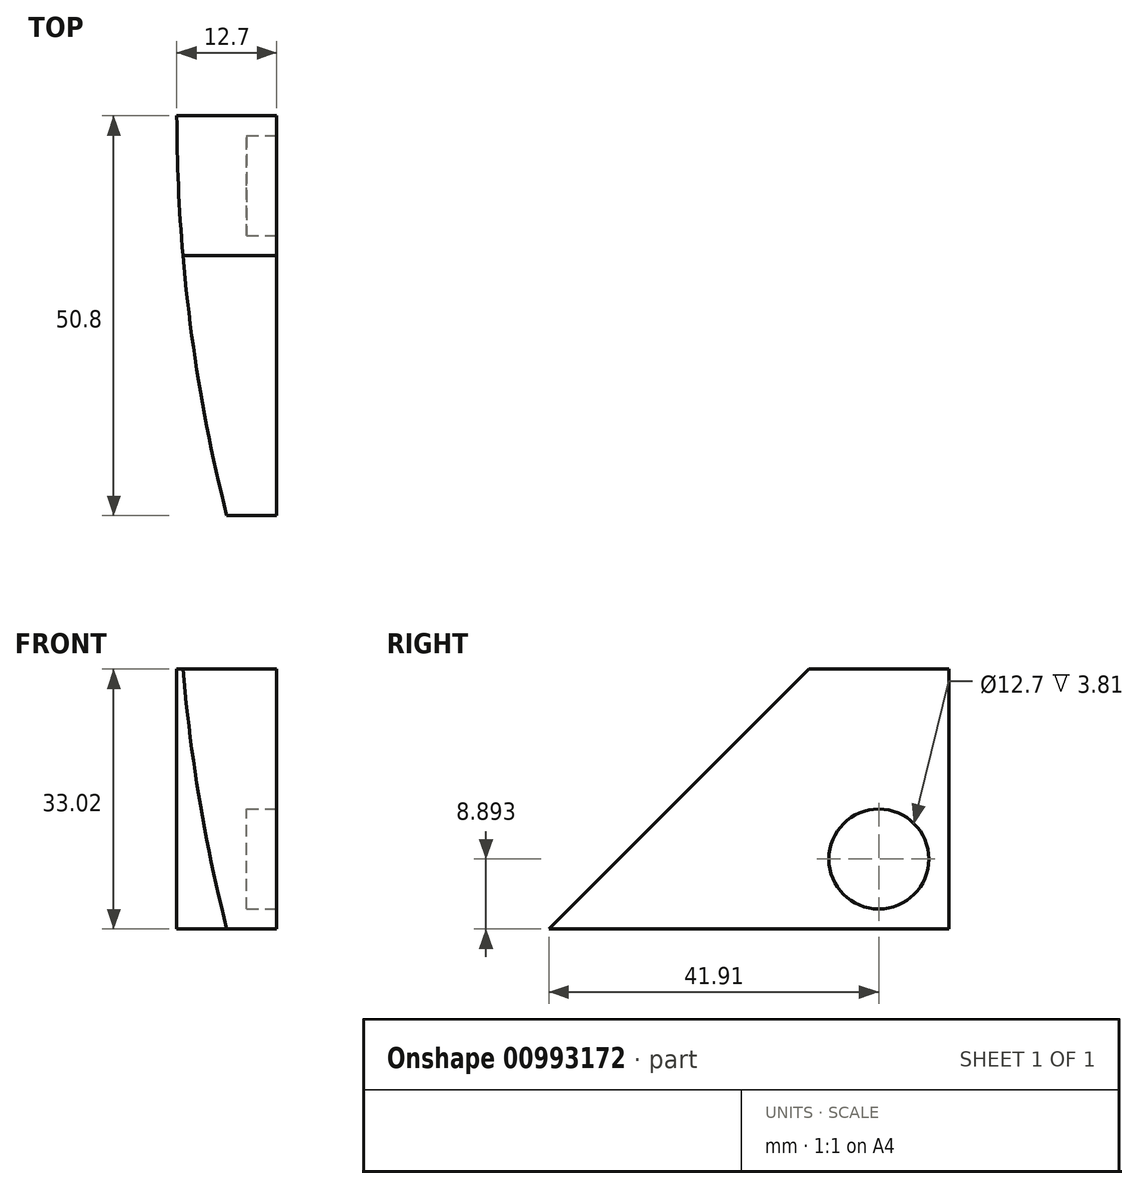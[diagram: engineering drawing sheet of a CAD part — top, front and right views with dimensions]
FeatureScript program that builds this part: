
annotation { "Feature Type Name" : "Feature", "Feature Type Description" : "" }
export const myFeature = defineFeature(function(context is Context, id is Id, definition is map)
    precondition{}
    {
        {
            var Q0;
            Q0=qCreatedBy(makeId("Right.planeOp"),FACE);
            var sketch = newSketch(context, id + "F0", { "sketchPlane" : qUnion([Q0])});
            skCircle(sketch, "E0", {"center": v(-28.5, 29.87) * mm, "radius": 6.35 * mm});
            skLineSegment(sketch, "E1.top", {"start": v(-70.4, 20.98) * mm, "end": v(-19.6, 20.98) * mm});
            skLineSegment(sketch, "E1.right", {"start": v(-19.6, 54) * mm, "end": v(-19.6, 20.98) * mm});
            skLineSegment(sketch, "E2", {"start": v(-70.4, 20.98) * mm, "end": v(-37.38, 54) * mm});
            skLineSegment(sketch, "E3", {"start": v(-37.38, 54) * mm, "end": v(-19.6, 54) * mm});
            skSolve(sketch);
        }
        {
            var Q0;
            Q0=makeQuery(id+"F0.imprint","IMPRINT",FACE,{"disambiguationData":[TD([[makeQuery(id+"F0.imprint","IMPRINT",EDGE,{"derivedFrom":sQuery(id+"F0.wireOp",EDGE,"E0")}),-1.0]])]});
            var Q1;
            Q1=makeQuery(id+"F0.imprint","IMPRINT",FACE,{"disambiguationData":[TD([[makeQuery(id+"F0.imprint","IMPRINT",EDGE,{"derivedFrom":sQuery(id+"F0.wireOp",EDGE,"E0")}),1.0]])]});
            extrude(context, id + "F1", {"entities" : qUnion([Q0, Q1]), "oppositeDirection" : true, "depth" : 12.7 * mm, "offsetDistance" : 25.4 * mm});
        }
        {
            var Q0;
            Q0=makeQuery(id+"F0.imprint","IMPRINT",FACE,{"disambiguationData":[TD([[makeQuery(id+"F0.imprint","IMPRINT",EDGE,{"derivedFrom":sQuery(id+"F0.wireOp",EDGE,"E0")}),1.0]])]});
            extrude(context, id + "F2", {"entities" : qUnion([Q0]), "operationType" : NewBodyOperationType.REMOVE, "oppositeDirection" : true, "depth" : 3.8 * mm, "offsetDistance" : 25.4 * mm});
        }
        {
            var Q0;
            Q0=makeQuery(id+"F1.opExtrude","SWEPT_FACE",FACE,{"disambiguationData":[OSD([sQuery(id+"F0.wireOp",EDGE,"E1.top")])]});
            var sketch = newSketch(context, id + "F3", { "sketchPlane" : qUnion([Q0])});
            skArc(sketch, "E4", {"start": v(-6.35, 70.4) * mm, "mid": v(-11.1, 45.2) * mm, "end": v(-12.7, 19.6) * mm});
            skSolve(sketch);
        }
        {
            var Q0;
            {var subQ0=sQuery(id+"F3.wireOp",EDGE,"E4");Q0=makeQuery(id+"F3.imprint","IMPRINT",FACE,{"disambiguationData":[TD([[makeQuery(id+"F3.imprint","IMPRINT",EDGE,{"derivedFrom":subQ0}),-1.0]])]});}
            extrude(context, id + "F4", {"entities" : qUnion([Q0]), "operationType" : NewBodyOperationType.REMOVE, "oppositeDirection" : true, "depth" : 50.8 * mm, "offsetDistance" : 25.4 * mm});
        }
    });
